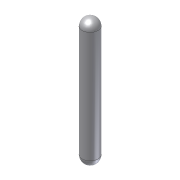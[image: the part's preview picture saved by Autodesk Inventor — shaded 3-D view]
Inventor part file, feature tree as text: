
AUTODESK INVENTOR PART (.ipt)
format: ipt  version: unknown  size: 164,864 bytes
history: native  units: mm
features: extrude x1, fillet x1, sketch x1
ambient origin geometry x8: Origin, YZ Plane, XZ Plane, XY Plane, X Axis, Y Axis, Z Axis, Center Point
feature tree (3):
  extrude  "Extrusion1"  Depth=4.0mm TaperAngle=0.0deg
  fillet  "Fillet1"  Radius=0.25mm
  sketch  "Sketch1"  dims[d0=0.5mm d1=4.0mm d2=0.0mm d3=0.25mm]
